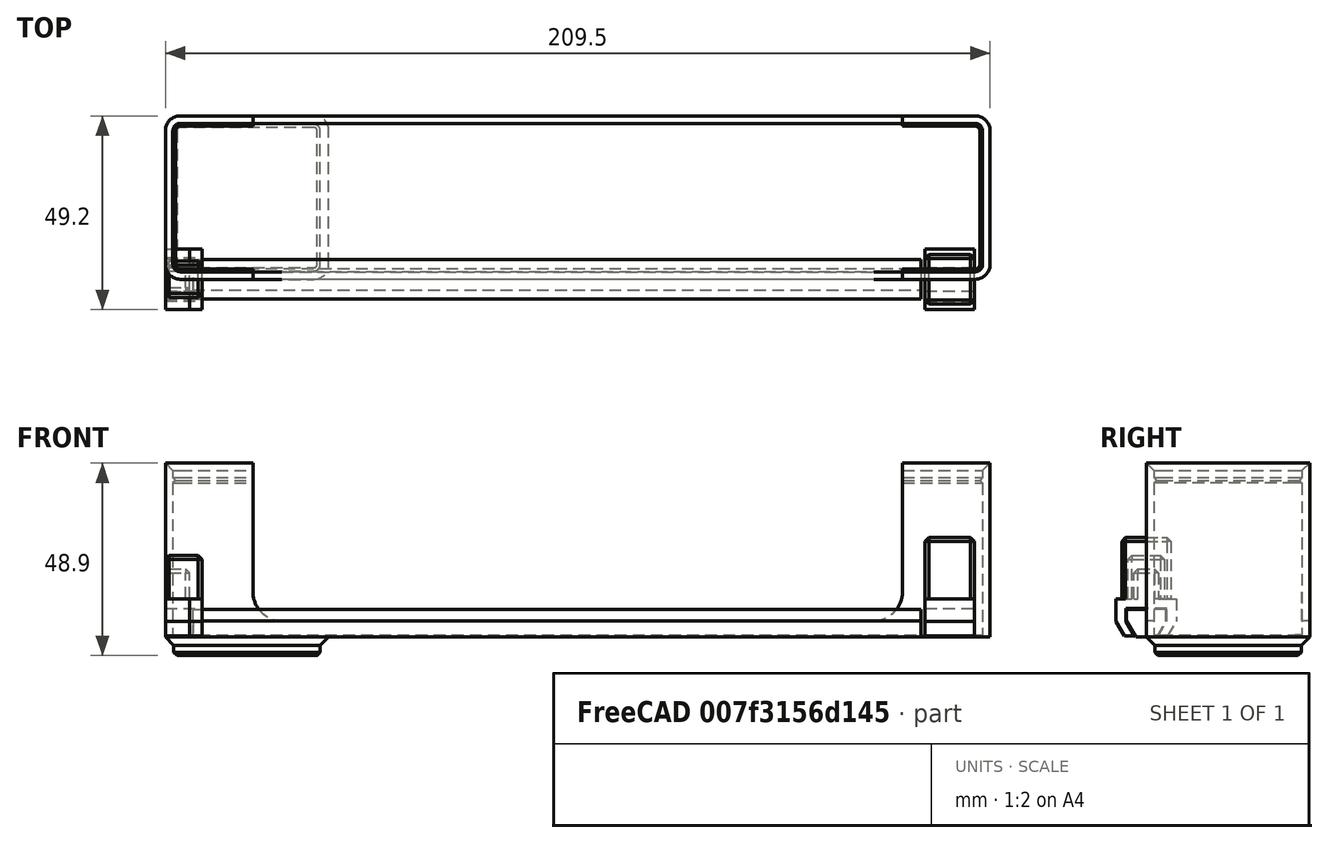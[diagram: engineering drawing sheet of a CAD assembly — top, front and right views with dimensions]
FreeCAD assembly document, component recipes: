
FREECAD ASSEMBLY — COMPONENT RECIPES ("GridfinityUniversalSocketHolder")

This assembly document has 3 components, labeled P0..P2 below (a component is one placed body or linked part). 3 of them carry a construction recipe — the FreeCAD feature program that regenerates the part from scratch, quoted from this document or its linked companion documents; the rest are supplied as boundary geometry only. No exploded tour is included for this assembly.
COMPONENT P0 — recipe-attached ("Part", modeled in this document).
Construction recipe (the document's own serialized feature program — sketch geometry with constraints, then the solid features built on it; lengths are millimeters unless a unit is written):

FEATURE [Sketcher::SketchObject] Sketch001  label="Path"
  FullyConstrained = true
  MapMode = 5
  Support = -> [XY_Plane001]
  sketch-geometry (10):
    g0: ArcOfCircle CenterX=3.75 CenterY=3.75 CenterZ=0 NormalX=0 NormalY=0 NormalZ=1 AngleXU=0 Radius=3.75 StartAngle=3.14159 EndAngle=4.71239
    g1: LineSegment StartX=1.15343e-11 StartY=3.75 StartZ=0 EndX=1.15343e-11 EndY=37.75 EndZ=0
    g2: ArcOfCircle CenterX=3.75 CenterY=37.75 CenterZ=0 NormalX=0 NormalY=0 NormalZ=1 AngleXU=0 Radius=3.75 StartAngle=1.5708 EndAngle=3.14159
    g3: LineSegment StartX=3.75 StartY=41.5 StartZ=0 EndX=37.75 EndY=41.5 EndZ=0
    g4: ArcOfCircle CenterX=37.75 CenterY=37.75 CenterZ=0 NormalX=0 NormalY=0 NormalZ=1 AngleXU=0 Radius=3.75 StartAngle=1.9105e-12 EndAngle=1.5708
    g5: LineSegment StartX=41.5 StartY=37.75 StartZ=0 EndX=41.5 EndY=3.75 EndZ=0
    g6: ArcOfCircle CenterX=37.75 CenterY=3.75 CenterZ=0 NormalX=0 NormalY=0 NormalZ=1 AngleXU=0 Radius=3.75 StartAngle=4.71239 EndAngle=6.28319
    g7: LineSegment StartX=37.75 StartY=1.15343e-11 StartZ=0 EndX=3.75 EndY=1.15343e-11 EndZ=0
    g8: GeomPoint X=0 Y=0 Z=0
    g9: GeomPoint X=41.5 Y=41.5 Z=0
  constraints (23):
    c: Tangent(g0,g1) = 1.5708
    c: Tangent(g1,g2) = 1.5708
    c: Tangent(g2,g3) = 1.5708
    c: Tangent(g3,g4) = 1.5708
    c: Tangent(g4,g5) = 1.5708
    c: Tangent(g5,g6) = 1.5708
    c: Tangent(g6,g7) = 1.5708
    c: Tangent(g7,g0) = 1.5708
    c: Horizontal(g3)
    c: Horizontal(g7)
    c: Vertical(g1)
    c: Vertical(g5)
    c: Equal(g0,g2)
    c: Equal(g2,g4)
    c: Equal(g4,g6)
    c: PointOnObject(g8,g1)
    c: PointOnObject(g8,g7)
    c: PointOnObject(g9,g3)
    c: PointOnObject(g9,g5)
    c: Coincident(g8,g-1)
    c: DistanceX(g1,g4) = 41.5
    c: DistanceY(g6,g3) = 41.5
    c: Diameter(g4) = 7.5
FEATURE [Sketcher::SketchObject] Sketch  label="1UProfile"
  FullyConstrained = true
  MapMode = 7
  Placement = pos=(37.75,1.15343e-11,0) rot=(0.57735,-0.57735,-0.57735;2.0944rad)
  Support = -> [Sketch001]
  sketch-geometry (5):
    g0: LineSegment StartX=-2.95 StartY=-4.75 StartZ=0 EndX=-2.15 EndY=-3.95 EndZ=0
    g1: LineSegment StartX=-2.15 StartY=-3.95 StartZ=0 EndX=-2.15 EndY=-2.15 EndZ=0
    g2: LineSegment StartX=-2.15 StartY=-2.15 StartZ=0 EndX=0 EndY=0 EndZ=0
    g3: LineSegment StartX=0 StartY=0 StartZ=0 EndX=-2.95 EndY=0 EndZ=0
    g4: LineSegment StartX=-2.95 StartY=0 StartZ=0 EndX=-2.95 EndY=-4.75 EndZ=0
  constraints (14):
    c: Vertical(g1)
    c: DistanceX(g1,g2) = 2.15
    c: DistanceY(g1,g2) = 2.15
    c: Distance(g1) = 1.8
    c: DistanceY(g0,g0) = 0.8
    c: DistanceX(g0,g0) = 0.8
    c: Coincident(g0,g1)
    c: Coincident(g1,g2)
    c: Coincident(g2,g3)
    c: Horizontal(g3)
    c: Coincident(g3,g4)
    c: Coincident(g4,g0)
    c: Vertical(g4)
    c: Coincident(g2,g-1)
FEATURE [PartDesign::AdditivePipe] AdditivePipe
  AuxilleryCurvelinear = true
  AuxillerySpineTangent = false
  Binormal = (0,0,0)
  Mode = 0
  Profile = -> Sketch
  Spine = -> Sketch001
  SpineTangent = false
  Transformation = 0
  Transition = 0
FEATURE [Sketcher::SketchObject] Sketch003
  FullyConstrained = true
  MapMode = 2
  Support = -> [AdditivePipe]
  expr: Constraints[21] = 2.15 + 0.8
  sketch-geometry (10):
    g0: ArcOfCircle CenterX=3.75 CenterY=37.75 CenterZ=0 NormalX=0 NormalY=0 NormalZ=1 AngleXU=0 Radius=0.8 StartAngle=1.5708 EndAngle=3.14159
    g1: LineSegment StartX=3.75 StartY=38.55 StartZ=0 EndX=37.75 EndY=38.55 EndZ=0
    g2: ArcOfCircle CenterX=37.75 CenterY=37.75 CenterZ=0 NormalX=0 NormalY=0 NormalZ=1 AngleXU=0 Radius=0.8 StartAngle=1.107e-13 EndAngle=1.5708
    g3: LineSegment StartX=38.55 StartY=37.75 StartZ=0 EndX=38.55 EndY=3.75 EndZ=0
    g4: ArcOfCircle CenterX=37.75 CenterY=3.75 CenterZ=0 NormalX=0 NormalY=0 NormalZ=1 AngleXU=0 Radius=0.8 StartAngle=4.71239 EndAngle=6.28319
    g5: LineSegment StartX=37.75 StartY=2.95 StartZ=0 EndX=3.75 EndY=2.95 EndZ=0
    g6: ArcOfCircle CenterX=3.75 CenterY=3.75 CenterZ=0 NormalX=0 NormalY=0 NormalZ=1 AngleXU=0 Radius=0.8 StartAngle=3.14159 EndAngle=4.71239
    g7: LineSegment StartX=2.95 StartY=3.75 StartZ=0 EndX=2.95 EndY=37.75 EndZ=0
    g8: GeomPoint X=2.95 Y=38.55 Z=0
    g9: GeomPoint X=38.55 Y=2.95 Z=0
  constraints (24):
    c: Tangent(g0,g1) = 1.5708
    c: Tangent(g1,g2) = 1.5708
    c: Tangent(g2,g3) = 1.5708
    c: Tangent(g3,g4) = 1.5708
    c: Tangent(g4,g5) = 1.5708
    c: Tangent(g5,g6) = 1.5708
    c: Tangent(g6,g7) = 1.5708
    c: Tangent(g7,g0) = 1.5708
    c: Horizontal(g1)
    c: Horizontal(g5)
    c: Vertical(g3)
    c: Vertical(g7)
    c: Equal(g0,g2)
    c: Equal(g2,g4)
    c: Equal(g4,g6)
    c: PointOnObject(g8,g1)
    c: PointOnObject(g8,g7)
    c: PointOnObject(g9,g3)
    c: PointOnObject(g9,g5)
    c: DistanceX(g0,g2) = 35.6
    c: DistanceY(g4,g1) = 35.6
    c: DistanceX(g-1,g6) = 2.95
    c: DistanceY(g-1,g5) = 2.95
    c: Diameter(g0) = 1.6
FEATURE [PartDesign::Pad] Pad
  BaseFeature = -> AdditivePipe
  Direction = (0,0,1)
  Length = 4.75
  Length2 = 10
  Profile = -> Sketch003
  ReferenceAxis = -> Sketch003 [N_Axis]
  Reversed = true
  Type = 0
FEATURE [Sketcher::SketchObject] Sketch002
  AttachmentOffset = pos=(0,-41.5,0) rot=(0,0,1;0rad)
  FullyConstrained = true
  MapMode = 5
  Placement = pos=(0,41.5,-4.75) rot=(1,0,0;3.14159rad)
  Support = -> [Pad]
  expr: Constraints[5] = 2.15 + 0.8 + 4.8
  expr: Constraints[8] = 41.5 - 7.75
  sketch-geometry (4):
    g0: Circle CenterX=7.75 CenterY=7.75 CenterZ=0 NormalX=0 NormalY=0 NormalZ=1 AngleXU=0 Radius=3.25
    g1: Circle CenterX=33.75 CenterY=7.75 CenterZ=0 NormalX=0 NormalY=0 NormalZ=1 AngleXU=0 Radius=3.25
    g2: Circle CenterX=33.75 CenterY=33.75 CenterZ=0 NormalX=0 NormalY=0 NormalZ=1 AngleXU=0 Radius=3.25
    g3: Circle CenterX=7.75 CenterY=33.75 CenterZ=0 NormalX=0 NormalY=0 NormalZ=1 AngleXU=0 Radius=3.25
  constraints (12):
    c: Equal(g0,g1)
    c: Equal(g1,g2)
    c: Equal(g2,g3)
    c: Diameter(g0) = 6.5
    c: DistanceX(g-1,g0) = 7.75
    c: DistanceY(g-1,g0) = 7.75
    c: DistanceX(g-1,g3) = 7.75
    c: DistanceY(g-1,g1) = 7.75
    c: DistanceY(g-1,g3) = 33.75
    c: DistanceX(g-1,g1) = 33.75
    c: DistanceX(g-1,g2) = 33.75
    c: DistanceY(g-1,g2) = 33.75
FEATURE [PartDesign::Pocket] Pocket
  BaseFeature = -> Pad
  Direction = (0,0,1)
  Length = 2.1
  Length2 = 5
  Profile = -> Sketch002
  ReferenceAxis = -> Sketch002 [N_Axis]
  Type = 0
FEATURE [PartDesign::Body] Body  label="1U Box Base"
  Group = -> [Sketch,Sketch001,AdditivePipe,Sketch003,Pad,Pocket,Sketch002]
  Origin = -> Origin001
  Tip = -> Pad
COMPONENT P1 — recipe-attached ("Rev2", modeled in this document).
Construction recipe (the document's own serialized feature program — sketch geometry with constraints, then the solid features built on it; lengths are millimeters unless a unit is written):

FEATURE [Sketcher::SketchObject] Sketch006
  FullyConstrained = true
  MapMode = 5
  Placement = pos=(0,0,0) rot=(0.57735,0.57735,0.57735;2.0944rad)
  Support = -> [YZ_Plane008]
  sketch-geometry (6):
    g0: LineSegment StartX=-5 StartY=4 StartZ=0 EndX=-2.6906 EndY=0 EndZ=0
    g1: LineSegment StartX=-2.6906 StartY=0 StartZ=0 EndX=2.6906 EndY=0 EndZ=0
    g2: LineSegment StartX=2.6906 StartY=0 StartZ=0 EndX=5 EndY=4 EndZ=0
    g3: LineSegment StartX=5 StartY=4 StartZ=0 EndX=5 EndY=7 EndZ=0
    g4: LineSegment StartX=5 StartY=7 StartZ=0 EndX=-5 EndY=7 EndZ=0
    g5: LineSegment StartX=-5 StartY=7 StartZ=0 EndX=-5 EndY=4 EndZ=0
  constraints (16):
    c: PointOnObject(g0,g-1)
    c: Coincident(g0,g1)
    c: Coincident(g1,g2)
    c: Coincident(g2,g3)
    c: Vertical(g3)
    c: Coincident(g3,g4)
    c: Coincident(g4,g5)
    c: Coincident(g5,g0)
    c: Vertical(g5)
    c: Symmetric(g3,g4,g-2)
    c: Symmetric(g0,g1,g-2)
    c: Equal(g3,g5)
    c: Angle(g2,g1) = 2.0944
    c: DistanceY(g3,g3) = 3
    c: DistanceY(g1,g2) = 4
    c: DistanceX(g4,g4) = 10
FEATURE [PartDesign::Pad] Pad004
  Direction = (1,-2e-16,3e-16)
  Length = 185
  Length2 = 10
  Placement = pos=(0,0,0) rot=(0.57735,0.57735,0.57735;2.0944rad)
  Profile = -> Sketch006
  ReferenceAxis = -> Sketch006 [N_Axis]
  Type = 0
FEATURE [PartDesign::ShapeBinder] ShapeBinder003
  Placement = pos=(0,0,0) rot=(0.57735,0.57735,0.57735;2.0944rad)
  Support = -> [Sketch006]
  TraceSupport = false
FEATURE [Sketcher::SketchObject] Sketch007
  ExternalGeometry = -> [ShapeBinder003]
  FullyConstrained = true
  MapMode = 5
  Placement = pos=(0,0,0) rot=(0.57735,0.57735,0.57735;2.0944rad)
  Support = -> [YZ_Plane009]
  expr: Constraints[24] = Spreadsheet.width_1_4
  expr: Constraints[25] = Spreadsheet.height_1_4
  expr: Constraints[35] = Spreadsheet.tolerance
  expr: Constraints[36] = Spreadsheet.tolerance
  expr: Constraints[38] = Spreadsheet.tolerance
  expr: Constraints[39] = Spreadsheet.tolerance
  sketch-geometry (16):
    g0: LineSegment StartX=3.03701 StartY=0.2 StartZ=0 EndX=5.2 EndY=3.94641 EndZ=0
    g1: LineSegment StartX=5.2 StartY=3.94641 StartZ=0 EndX=5.2 EndY=7.2 EndZ=0
    g2: LineSegment StartX=5.2 StartY=7.2 StartZ=0 EndX=-5.2 EndY=7.2 EndZ=0
    g3: LineSegment StartX=-5.2 StartY=7.2 StartZ=0 EndX=-5.2 EndY=3.94641 EndZ=0
    g4: LineSegment StartX=-5.2 StartY=3.94641 StartZ=0 EndX=-3.03701 EndY=0.2 EndZ=0
    g5: LineSegment StartX=-3.03701 StartY=0.2 StartZ=0 EndX=-5.53701 EndY=0.2 EndZ=0
    g6: LineSegment StartX=-7.7 StartY=3.94641 StartZ=0 EndX=-7.7 EndY=9.7 EndZ=0
    g7: LineSegment StartX=-7.7 StartY=9.7 StartZ=0 EndX=-3.1 EndY=9.7 EndZ=0
    g8: LineSegment StartX=-3.1 StartY=9.7 StartZ=0 EndX=-3.1 EndY=17.3 EndZ=0
    g9: LineSegment StartX=-3.1 StartY=17.3 StartZ=0 EndX=3.1 EndY=17.3 EndZ=0
    g10: LineSegment StartX=3.1 StartY=17.3 StartZ=0 EndX=3.1 EndY=9.7 EndZ=0
    g11: LineSegment StartX=3.1 StartY=9.7 StartZ=0 EndX=7.7 EndY=9.7 EndZ=0
    g12: LineSegment StartX=7.7 StartY=9.7 StartZ=0 EndX=7.7 EndY=3.94641 EndZ=0
    g13: LineSegment StartX=5.53701 StartY=0.2 StartZ=0 EndX=3.03701 EndY=0.2 EndZ=0
    g14: LineSegment StartX=5.53701 StartY=0.2 StartZ=0 EndX=7.7 EndY=3.94641 EndZ=0
    g15: LineSegment StartX=-5.53701 StartY=0.2 StartZ=0 EndX=-7.7 EndY=3.94641 EndZ=0
  constraints (42):
    c: Coincident(g0,g1)
    c: Vertical(g1)
    c: Coincident(g1,g2)
    c: Coincident(g2,g3)
    c: Coincident(g3,g4)
    c: Coincident(g4,g5)
    c: Vertical(g6)
    c: Coincident(g6,g7)
    c: Horizontal(g7)
    c: Coincident(g7,g8)
    c: Vertical(g8)
    c: Coincident(g8,g9)
    c: Coincident(g9,g10)
    c: Vertical(g10)
    c: Coincident(g10,g11)
    c: Horizontal(g11)
    c: Coincident(g11,g12)
    c: Vertical(g12)
    c: Coincident(g13,g0)
    c: Symmetric(g9,g8,g-2)
    c: Symmetric(g11,g6,g-2)
    c: Symmetric(g2,g1,g-2)
    c: Symmetric(g3,g0,g-2)
    c: Symmetric(g4,g0,g-2)
    c: DistanceX(g9,g9) = 6.2
    c: DistanceY(g10,g10) = 7.6
    c: Parallel(g0,g-5)
    c: Parallel(g14,g0)
    c: Symmetric(g14,g15,g-2)
    c: Symmetric(g14,g15,g-2)
    c: DistanceX(g15,g4) = 2.5
    c: PointOnObject(g6,g15)
    c: Coincident(g12,g14)
    c: Coincident(g13,g14)
    c: Symmetric(g13,g5,g-2)
    c: DistanceX(g-4,g1) = 0.2
    c: DistanceY(g-1,g13) = 0.2
    c: Horizontal(g5)
    c: Distance(g0,g-5) = 0.2
    c: DistanceY(g-4,g1) = 0.2
    c: DistanceY(g2,g6) = 2.5
    c: DistanceX(g6,g2) = 2.5
FEATURE [PartDesign::Pad] Pad005
  Direction = (1,-2e-16,3e-16)
  Length = 6.2
  Length2 = 10
  Placement = pos=(0,0,0) rot=(0.57735,0.57735,0.57735;2.0944rad)
  Profile = -> Sketch007
  ReferenceAxis = -> Sketch007 [N_Axis]
  Type = 0
  expr: Length = Spreadsheet.width_1_4
FEATURE [PartDesign::Chamfer] Chamfer011
  Angle = 45
  Base = -> Pad005 [Face12,Edge39,Edge40,Edge33,Edge34]
  BaseFeature = -> Pad005
  ChamferType = 0
  FlipDirection = false
  Placement = pos=(0,0,0) rot=(0.57735,0.57735,0.57735;2.0944rad)
  Size = 1
  Size2 = 1
  SupportTransform = false
  UseAllEdges = false
FEATURE [PartDesign::Body] Body005  label="1/4 Socket Stud"
  Group = -> [ShapeBinder003,Sketch007,Pad005,Chamfer011]
  Origin = -> Origin007
  Tip = -> Chamfer011
FEATURE [PartDesign::ShapeBinder] ShapeBinder004
  Placement = pos=(0,0,0) rot=(0.57735,0.57735,0.57735;2.0944rad)
  Support = -> [Sketch006]
  TraceSupport = false
FEATURE [Sketcher::SketchObject] Sketch008
  ExternalGeometry = -> [ShapeBinder004]
  FullyConstrained = true
  MapMode = 5
  Placement = pos=(0,0,0) rot=(0.57735,0.57735,0.57735;2.0944rad)
  Support = -> [YZ_Plane010]
  expr: Constraints[24] = Spreadsheet.width_3_8
  expr: Constraints[25] = Spreadsheet.height_3_8
  expr: Constraints[35] = Spreadsheet.tolerance
  expr: Constraints[36] = Spreadsheet.tolerance
  expr: Constraints[38] = Spreadsheet.tolerance
  expr: Constraints[39] = Spreadsheet.tolerance
  sketch-geometry (16):
    g0: LineSegment StartX=3.03701 StartY=0.2 StartZ=0 EndX=5.2 EndY=3.94641 EndZ=0
    g1: LineSegment StartX=5.2 StartY=3.94641 StartZ=0 EndX=5.2 EndY=7.2 EndZ=0
    g2: LineSegment StartX=5.2 StartY=7.2 StartZ=0 EndX=-5.2 EndY=7.2 EndZ=0
    g3: LineSegment StartX=-5.2 StartY=7.2 StartZ=0 EndX=-5.2 EndY=3.94641 EndZ=0
    g4: LineSegment StartX=-5.2 StartY=3.94641 StartZ=0 EndX=-3.03701 EndY=0.2 EndZ=0
    g5: LineSegment StartX=-3.03701 StartY=0.2 StartZ=0 EndX=-5.53701 EndY=0.2 EndZ=0
    g6: LineSegment StartX=-7.7 StartY=3.94641 StartZ=0 EndX=-7.7 EndY=9.7 EndZ=0
    g7: LineSegment StartX=-7.7 StartY=9.7 StartZ=0 EndX=-4.65 EndY=9.7 EndZ=0
    g8: LineSegment StartX=-4.65 StartY=9.7 StartZ=0 EndX=-4.65 EndY=20.7 EndZ=0
    g9: LineSegment StartX=-4.65 StartY=20.7 StartZ=0 EndX=4.65 EndY=20.7 EndZ=0
    g10: LineSegment StartX=4.65 StartY=20.7 StartZ=0 EndX=4.65 EndY=9.7 EndZ=0
    g11: LineSegment StartX=4.65 StartY=9.7 StartZ=0 EndX=7.7 EndY=9.7 EndZ=0
    g12: LineSegment StartX=7.7 StartY=9.7 StartZ=0 EndX=7.7 EndY=3.94641 EndZ=0
    g13: LineSegment StartX=5.53701 StartY=0.2 StartZ=0 EndX=3.03701 EndY=0.2 EndZ=0
    g14: LineSegment StartX=5.53701 StartY=0.2 StartZ=0 EndX=7.7 EndY=3.94641 EndZ=0
    g15: LineSegment StartX=-5.53701 StartY=0.2 StartZ=0 EndX=-7.7 EndY=3.94641 EndZ=0
  constraints (42):
    c: Coincident(g0,g1)
    c: Vertical(g1)
    c: Coincident(g1,g2)
    c: Coincident(g2,g3)
    c: Coincident(g3,g4)
    c: Coincident(g4,g5)
    c: Vertical(g6)
    c: Coincident(g6,g7)
    c: Horizontal(g7)
    c: Coincident(g7,g8)
    c: Vertical(g8)
    c: Coincident(g8,g9)
    c: Coincident(g9,g10)
    c: Vertical(g10)
    c: Coincident(g10,g11)
    c: Horizontal(g11)
    c: Coincident(g11,g12)
    c: Vertical(g12)
    c: Coincident(g13,g0)
    c: Symmetric(g9,g8,g-2)
    c: Symmetric(g11,g6,g-2)
    c: Symmetric(g2,g1,g-2)
    c: Symmetric(g3,g0,g-2)
    c: Symmetric(g4,g0,g-2)
    c: DistanceX(g9,g9) = 9.3
    c: DistanceY(g10,g10) = 11
    c: Parallel(g0,g-5)
    c: Parallel(g14,g0)
    c: Symmetric(g14,g15,g-2)
    c: Symmetric(g14,g15,g-2)
    c: DistanceX(g15,g4) = 2.5
    c: PointOnObject(g6,g15)
    c: Coincident(g12,g14)
    c: Coincident(g13,g14)
    c: Symmetric(g13,g5,g-2)
    c: DistanceX(g-4,g1) = 0.2
    c: DistanceY(g-1,g13) = 0.2
    c: Horizontal(g5)
    c: Distance(g0,g-5) = 0.2
    c: DistanceY(g-4,g1) = 0.2
    c: DistanceY(g2,g6) = 2.5
    c: DistanceX(g6,g2) = 2.5
FEATURE [PartDesign::Pad] Pad006
  Direction = (1,-2e-16,3e-16)
  Length = 9.3
  Length2 = 10
  Placement = pos=(0,0,0) rot=(0.57735,0.57735,0.57735;2.0944rad)
  Profile = -> Sketch008
  ReferenceAxis = -> Sketch008 [N_Axis]
  Type = 0
  expr: Length = Spreadsheet.width_3_8
FEATURE [PartDesign::Chamfer] Chamfer012
  Angle = 45
  Base = -> Pad006 [Face12,Edge39,Edge40,Edge33,Edge34]
  BaseFeature = -> Pad006
  ChamferType = 0
  FlipDirection = false
  Placement = pos=(0,0,0) rot=(0.57735,0.57735,0.57735;2.0944rad)
  Size = 1
  Size2 = 1
  SupportTransform = false
  UseAllEdges = false
FEATURE [PartDesign::Body] Body006  label="3/8 Socket Stud"
  Group = -> [ShapeBinder004,Sketch008,Pad006,Chamfer012]
  Origin = -> Origin008
  Tip = -> Chamfer012
FEATURE [PartDesign::ShapeBinder] ShapeBinder005
  Placement = pos=(0,0,0) rot=(0.57735,0.57735,0.57735;2.0944rad)
  Support = -> [Sketch006]
  TraceSupport = false
FEATURE [Sketcher::SketchObject] Sketch009
  ExternalGeometry = -> [ShapeBinder005]
  FullyConstrained = true
  MapMode = 5
  Placement = pos=(0,0,0) rot=(0.57735,0.57735,0.57735;2.0944rad)
  Support = -> [YZ_Plane011]
  expr: Constraints[24] = Spreadsheet.width_1_2
  expr: Constraints[25] = Spreadsheet.height_1_2
  expr: Constraints[35] = Spreadsheet.tolerance
  expr: Constraints[36] = Spreadsheet.tolerance
  expr: Constraints[38] = Spreadsheet.tolerance
  expr: Constraints[39] = Spreadsheet.tolerance
  sketch-geometry (16):
    g0: LineSegment StartX=3.03701 StartY=0.2 StartZ=0 EndX=5.2 EndY=3.94641 EndZ=0
    g1: LineSegment StartX=5.2 StartY=3.94641 StartZ=0 EndX=5.2 EndY=7.2 EndZ=0
    g2: LineSegment StartX=5.2 StartY=7.2 StartZ=0 EndX=-5.2 EndY=7.2 EndZ=0
    g3: LineSegment StartX=-5.2 StartY=7.2 StartZ=0 EndX=-5.2 EndY=3.94641 EndZ=0
    g4: LineSegment StartX=-5.2 StartY=3.94641 StartZ=0 EndX=-3.03701 EndY=0.2 EndZ=0
    g5: LineSegment StartX=-3.03701 StartY=0.2 StartZ=0 EndX=-5.53701 EndY=0.2 EndZ=0
    g6: LineSegment StartX=-7.7 StartY=3.94641 StartZ=0 EndX=-7.7 EndY=9.7 EndZ=0
    g7: LineSegment StartX=-7.7 StartY=9.7 StartZ=0 EndX=-6.25 EndY=9.7 EndZ=0
    g8: LineSegment StartX=-6.25 StartY=9.7 StartZ=0 EndX=-6.25 EndY=25.3 EndZ=0
    g9: LineSegment StartX=-6.25 StartY=25.3 StartZ=0 EndX=6.25 EndY=25.3 EndZ=0
    g10: LineSegment StartX=6.25 StartY=25.3 StartZ=0 EndX=6.25 EndY=9.7 EndZ=0
    g11: LineSegment StartX=6.25 StartY=9.7 StartZ=0 EndX=7.7 EndY=9.7 EndZ=0
    g12: LineSegment StartX=7.7 StartY=9.7 StartZ=0 EndX=7.7 EndY=3.94641 EndZ=0
    g13: LineSegment StartX=5.53701 StartY=0.2 StartZ=0 EndX=3.03701 EndY=0.2 EndZ=0
    g14: LineSegment StartX=5.53701 StartY=0.2 StartZ=0 EndX=7.7 EndY=3.94641 EndZ=0
    g15: LineSegment StartX=-5.53701 StartY=0.2 StartZ=0 EndX=-7.7 EndY=3.94641 EndZ=0
  constraints (42):
    c: Coincident(g0,g1)
    c: Vertical(g1)
    c: Coincident(g1,g2)
    c: Coincident(g2,g3)
    c: Coincident(g3,g4)
    c: Coincident(g4,g5)
    c: Vertical(g6)
    c: Coincident(g6,g7)
    c: Horizontal(g7)
    c: Coincident(g7,g8)
    c: Vertical(g8)
    c: Coincident(g8,g9)
    c: Coincident(g9,g10)
    c: Vertical(g10)
    c: Coincident(g10,g11)
    c: Horizontal(g11)
    c: Coincident(g11,g12)
    c: Vertical(g12)
    c: Coincident(g13,g0)
    c: Symmetric(g9,g8,g-2)
    c: Symmetric(g11,g6,g-2)
    c: Symmetric(g2,g1,g-2)
    c: Symmetric(g3,g0,g-2)
    c: Symmetric(g4,g0,g-2)
    c: DistanceX(g9,g9) = 12.5
    c: DistanceY(g10,g10) = 15.6
    c: Parallel(g0,g-5)
    c: Parallel(g14,g0)
    c: Symmetric(g14,g15,g-2)
    c: Symmetric(g14,g15,g-2)
    c: DistanceX(g15,g4) = 2.5
    c: PointOnObject(g6,g15)
    c: Coincident(g12,g14)
    c: Coincident(g13,g14)
    c: Symmetric(g13,g5,g-2)
    c: DistanceX(g-4,g1) = 0.2
    c: DistanceY(g-1,g13) = 0.2
    c: Horizontal(g5)
    c: Distance(g0,g-5) = 0.2
    c: DistanceY(g-4,g1) = 0.2
    c: DistanceY(g2,g6) = 2.5
    c: DistanceX(g6,g2) = 2.5
FEATURE [PartDesign::Pad] Pad007
  Direction = (1,-2e-16,3e-16)
  Length = 12.5
  Length2 = 10
  Placement = pos=(0,0,0) rot=(0.57735,0.57735,0.57735;2.0944rad)
  Profile = -> Sketch009
  ReferenceAxis = -> Sketch009 [N_Axis]
  Type = 0
  expr: Length = Spreadsheet.width_1_2
FEATURE [PartDesign::Chamfer] Chamfer013
  Angle = 45
  Base = -> Pad007 [Face12,Edge39,Edge40,Edge33,Edge34]
  BaseFeature = -> Pad007
  ChamferType = 0
  FlipDirection = false
  Placement = pos=(0,0,0) rot=(0.57735,0.57735,0.57735;2.0944rad)
  Size = 1
  Size2 = 1
  SupportTransform = false
  UseAllEdges = false
FEATURE [PartDesign::Body] Body007  label="1/2 Socket Stud"
  Group = -> [ShapeBinder005,Sketch009,Pad007,Chamfer013]
  Origin = -> Origin009
  Placement = pos=(193,0,0) rot=(0,0,1;0rad)
  Tip = -> Chamfer013
FEATURE [Sketcher::SketchObject] Sketch010
  FullyConstrained = true
  MapMode = 5
  Support = -> [XY_Plane006]
FEATURE [PartDesign::Body] Body004  label="Dovetail"
  Group = -> [Sketch006,Pad004,Sketch010]
  Origin = -> Origin006
  Placement = pos=(7,0,0) rot=(0,0,1;0rad)
  Tip = -> Pad004
COMPONENT P2 — recipe-attached ("Sides", modeled in this document).
Construction recipe (the document's own serialized feature program — sketch geometry with constraints, then the solid features built on it; lengths are millimeters unless a unit is written):

FEATURE [PartDesign::ShapeBinder] ShapeBinder
  Support = -> [Array]
  TraceSupport = false
FEATURE [Sketcher::SketchObject] Sketch011
  FullyConstrained = true
  MapMode = 5
  Support = -> [XY_Plane012]
  expr: Constraints[19] = 5 * 42 - 0.5
  sketch-geometry (10):
    g0: ArcOfCircle CenterX=3.75 CenterY=37.75 CenterZ=0 NormalX=0 NormalY=0 NormalZ=1 AngleXU=0 Radius=3.75 StartAngle=1.5708 EndAngle=3.14159
    g1: LineSegment StartX=3.75 StartY=41.5 StartZ=0 EndX=205.75 EndY=41.5 EndZ=0
    g2: ArcOfCircle CenterX=205.75 CenterY=37.75 CenterZ=0 NormalX=0 NormalY=0 NormalZ=1 AngleXU=0 Radius=3.75 StartAngle=8.262e-13 EndAngle=1.5708
    g3: LineSegment StartX=209.5 StartY=37.75 StartZ=0 EndX=209.5 EndY=3.75 EndZ=0
    g4: ArcOfCircle CenterX=205.75 CenterY=3.75 CenterZ=0 NormalX=0 NormalY=0 NormalZ=1 AngleXU=0 Radius=3.75 StartAngle=4.71239 EndAngle=6.28319
    g5: LineSegment StartX=205.75 StartY=1.08793e-11 StartZ=0 EndX=3.75 EndY=1.08793e-11 EndZ=0
    g6: ArcOfCircle CenterX=3.75 CenterY=3.75 CenterZ=0 NormalX=0 NormalY=0 NormalZ=1 AngleXU=0 Radius=3.75 StartAngle=3.14159 EndAngle=4.71239
    g7: LineSegment StartX=1.07767e-11 StartY=3.75 StartZ=0 EndX=1.07767e-11 EndY=37.75 EndZ=0
    g8: GeomPoint X=0 Y=41.5 Z=0
    g9: GeomPoint X=209.5 Y=0 Z=0
  constraints (24):
    c: Tangent(g0,g1) = 1.5708
    c: Tangent(g1,g2) = 1.5708
    c: Tangent(g2,g3) = 1.5708
    c: Tangent(g3,g4) = 1.5708
    c: Tangent(g4,g5) = 1.5708
    c: Tangent(g5,g6) = 1.5708
    c: Tangent(g6,g7) = 1.5708
    c: Tangent(g7,g0) = 1.5708
    c: Horizontal(g1)
    c: Horizontal(g5)
    c: Vertical(g3)
    c: Vertical(g7)
    c: Equal(g0,g2)
    c: Equal(g2,g4)
    c: Equal(g4,g6)
    c: PointOnObject(g8,g1)
    c: PointOnObject(g8,g7)
    c: PointOnObject(g9,g3)
    c: PointOnObject(g9,g5)
    c: DistanceX(g6,g3) = 209.5
    c: PointOnObject(g6,g-2)
    c: PointOnObject(g5,g-1)
    c: DistanceY(g5,g0) = 41.5
    c: Diameter(g0) = 7.5
FEATURE [PartDesign::Pad] Pad008
  Direction = (0,0,1)
  Length = 0.5
  Length2 = 10
  Profile = -> Sketch011
  ReferenceAxis = -> Sketch011 [N_Axis]
  Type = 0
FEATURE [Sketcher::SketchObject] Sketch012
  FullyConstrained = true
  MapMode = 7
  Placement = pos=(205.75,1.08793e-11,0.5) rot=(0.57735,0.57735,0.57735;2.0944rad)
  Support = -> [Pad008]
  expr: Constraints[19] = 4.25 + 7 * 5
  sketch-geometry (7):
    g0: LineSegment StartX=0 StartY=0 StartZ=0 EndX=0 EndY=43.65 EndZ=0
    g1: LineSegment StartX=0 StartY=43.65 StartZ=0 EndX=1.9 EndY=41.75 EndZ=0
    g2: LineSegment StartX=1.9 StartY=41.75 StartZ=0 EndX=1.9 EndY=39.95 EndZ=0
    g3: LineSegment StartX=1.9 StartY=39.95 StartZ=0 EndX=2.6 EndY=39.25 EndZ=0
    g4: LineSegment StartX=2.6 StartY=39.25 StartZ=0 EndX=1.9 EndY=38.55 EndZ=0
    g5: LineSegment StartX=1.9 StartY=38.55 StartZ=0 EndX=1.9 EndY=0 EndZ=0
    g6: LineSegment StartX=1.9 StartY=0 StartZ=0 EndX=0 EndY=0 EndZ=0
  constraints (20):
    c: Coincident(g-1,g0)
    c: PointOnObject(g0,g-2)
    c: Coincident(g0,g1)
    c: Coincident(g1,g2)
    c: Vertical(g2)
    c: Coincident(g2,g3)
    c: Coincident(g3,g4)
    c: Coincident(g4,g5)
    c: PointOnObject(g5,g-1)
    c: Vertical(g5)
    c: Coincident(g5,g6)
    c: Coincident(g6,g0)
    c: Angle(g0,g1) = 0.785398
    c: Parallel(g1,g3)
    c: Vertical(g4,g2)
    c: DistanceY(g1,g0) = 1.9
    c: DistanceY(g3,g2) = 0.7
    c: Perpendicular(g4,g3)
    c: DistanceY(g2,g2) = 1.8
    c: DistanceY(g0,g3) = 39.25
FEATURE [PartDesign::AdditivePipe] AdditivePipe001
  AuxilleryCurvelinear = true
  AuxillerySpineTangent = false
  BaseFeature = -> Pad008
  Binormal = (0,0,0)
  Mode = 0
  Profile = -> Sketch012
  Spine = -> Pad008 [Edge13,Edge16,Edge19,Edge22,Edge24,Edge4,Edge7,Edge10]
  SpineTangent = false
  Transformation = 0
  Transition = 0
FEATURE [Sketcher::SketchObject] Sketch013
  ExternalGeometry = -> [AdditivePipe001]
  FullyConstrained = true
  MapMode = 5
  Placement = pos=(0,1.08793e-11,0) rot=(1,0,0;1.5708rad)
  Support = -> [AdditivePipe001]
  sketch-geometry (8):
    g0: LineSegment StartX=22.25 StartY=44.15 StartZ=0 EndX=187.25 EndY=44.15 EndZ=0
    g1: LineSegment StartX=187.25 StartY=44.15 StartZ=0 EndX=187.25 EndY=11.4 EndZ=0
    g2: LineSegment StartX=180 StartY=4.15 StartZ=0 EndX=29.5 EndY=4.15 EndZ=0
    g3: LineSegment StartX=22.25 StartY=11.4 StartZ=0 EndX=22.25 EndY=44.15 EndZ=0
    g4: ArcOfCircle CenterX=29.5 CenterY=11.4 CenterZ=0 NormalX=0 NormalY=0 NormalZ=1 AngleXU=0 Radius=7.25 StartAngle=3.14159 EndAngle=4.71239
    g5: ArcOfCircle CenterX=180 CenterY=11.4 CenterZ=0 NormalX=0 NormalY=0 NormalZ=1 AngleXU=0 Radius=7.25 StartAngle=4.71239 EndAngle=6.28319
    g6: LineSegment StartX=3.75 StartY=44.15 StartZ=0 EndX=22.25 EndY=44.15 EndZ=0
    g7: LineSegment StartX=187.25 StartY=44.15 StartZ=0 EndX=205.75 EndY=44.15 EndZ=0
  constraints (20):
    c: Coincident(g0,g1)
    c: Coincident(g3,g0)
    c: Horizontal(g0)
    c: Horizontal(g2)
    c: Vertical(g1)
    c: Vertical(g3)
    c: PointOnObject(g0,g-3)
    c: Tangent(g2,g4) = 1.5708
    c: Tangent(g3,g4) = 1.5708
    c: Tangent(g1,g5) = 1.5708
    c: Tangent(g2,g5) = 1.5708
    c: Equal(g5,g4)
    c: DistanceX(g0,g0) = 165
    c: DistanceY(g2,g0) = 40
    c: Coincident(g6,g-3)
    c: Coincident(g6,g0)
    c: Coincident(g7,g0)
    c: Coincident(g7,g-3)
    c: Equal(g7,g6)
    c: Diameter(g5) = 14.5
FEATURE [PartDesign::Pocket] Pocket001
  BaseFeature = -> AdditivePipe001
  Direction = (0,1,-2e-16)
  Length = 0
  Length2 = 5
  Profile = -> Sketch013
  ReferenceAxis = -> Sketch013 [N_Axis]
  Type = 3
  UpToFace = -> AdditivePipe001 [Face7]
FEATURE [PartDesign::Body] Body008
  Group = -> [ShapeBinder,Sketch011,Pad008,Sketch012,AdditivePipe001,Sketch013,Pocket001]
  Origin = -> Origin012
  Tip = -> Pocket001
PROVENANCE & LICENSES
A FreeCAD (.FCStd) document from a public repository crawl; recipes are the document's own serialized feature recipes (and, for linked parts, companion documents' recipes).
License: as declared in the source repository (recorded in the dataset sidecar).
